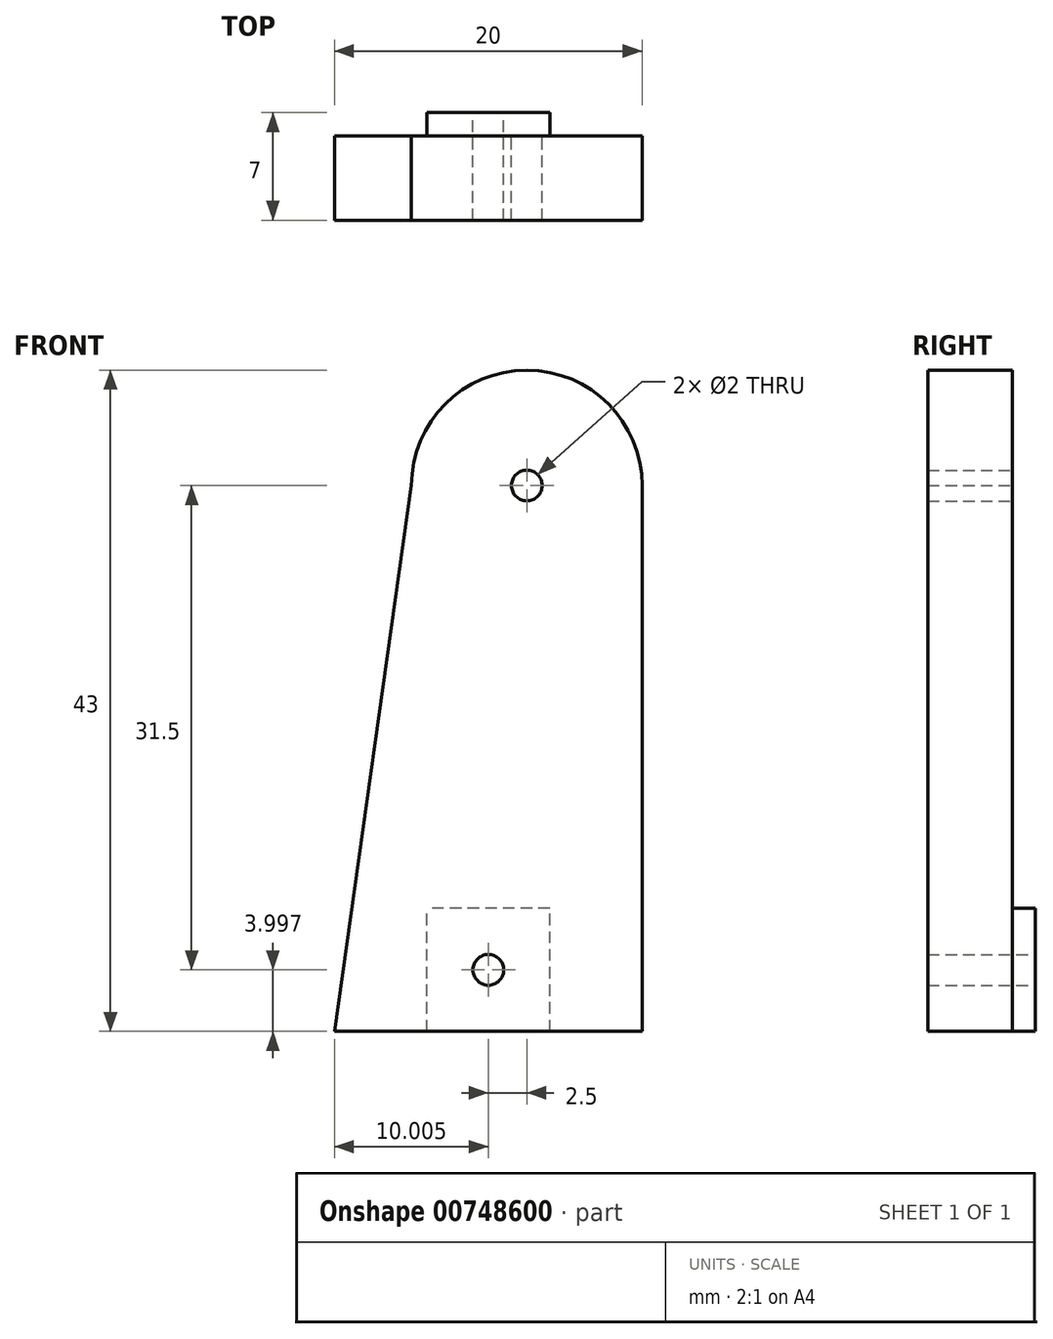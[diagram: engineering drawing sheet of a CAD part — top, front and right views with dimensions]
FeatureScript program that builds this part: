
annotation { "Feature Type Name" : "Feature", "Feature Type Description" : "" }
export const myFeature = defineFeature(function(context is Context, id is Id, definition is map)
    precondition{}
    {
        {
            var Q0;
            Q0=qCreatedBy(makeId("Front.planeOp"),FACE);
            var sketch = newSketch(context, id + "F0", { "sketchPlane" : qUnion([Q0])});
            skLineSegment(sketch, "E0.bottom", {"start": v(-52.7, 92.14) * mm, "end": v(-37.7, 92.14) * mm});
            skLineSegment(sketch, "E0.top", {"start": v(-52.7, -7.86) * mm, "end": v(-37.7, -7.86) * mm});
            skLineSegment(sketch, "E0.left", {"start": v(-52.7, 92.14) * mm, "end": v(-52.7, -7.86) * mm});
            skLineSegment(sketch, "E0.right", {"start": v(-37.7, 92.14) * mm, "end": v(-37.7, -7.86) * mm});
            skCircle(sketch, "E1", {"center": v(-45.2, 84.64) * mm, "radius": 1 * mm});
            skCircle(sketch, "E2", {"center": v(-45.2, 84.64) * mm, "radius": 7.5 * mm});
            skSolve(sketch);
        }
        {
            var Q0;
            Q0=makeQuery(id+"F0.imprint","IMPRINT",FACE,{"disambiguationData":[TD([[makeQuery(id+"F0.imprint","IMPRINT",EDGE,{"derivedFrom":sQuery(id+"F0.wireOp",EDGE,"E1")}),-1.0]])]});
            var Q1;
            {var subQ0=sQuery(id+"F0.wireOp",EDGE,"E0.top");Q1=makeQuery(id+"F0.imprint","IMPRINT",FACE,{"disambiguationData":[TD([[makeQuery(id+"F0.imprint","IMPRINT",EDGE,{"derivedFrom":subQ0}),1.0]])]});}
            extrude(context, id + "F1", {"entities" : qUnion([Q0, Q1]), "depth" : 5.5 * mm, "offsetDistance" : 25 * mm});
        }
        {
            var Q0;
            Q0=makeQuery(id+"F1.opExtrude","SWEPT_FACE",FACE,{"disambiguationData":[OSD([sQuery(id+"F0.wireOp",EDGE,"E0.left")])]});
            var sketch = newSketch(context, id + "F2", { "sketchPlane" : qUnion([Q0])});
            skLineSegment(sketch, "E3.bottom", {"start": v(0, 84.64) * mm, "end": v(5.5, 84.64) * mm});
            skLineSegment(sketch, "E3.top", {"start": v(0, 49.14) * mm, "end": v(5.5, 49.14) * mm});
            skLineSegment(sketch, "E3.left", {"start": v(0, 84.64) * mm, "end": v(0, 49.14) * mm});
            skLineSegment(sketch, "E3.right", {"start": v(5.5, 84.64) * mm, "end": v(5.5, 49.14) * mm});
            skSolve(sketch);
        }
        {
            var Q0;
            {var subQ0=sQuery(id+"F2.wireOp",EDGE,"E3.top");Q0=makeQuery(id+"F2.imprint","IMPRINT",FACE,{"disambiguationData":[TD([[makeQuery(id+"F2.imprint","IMPRINT",EDGE,{"derivedFrom":subQ0}),-1.0]])]});}
            extrude(context, id + "F3", {"entities" : qUnion([Q0]), "operationType" : NewBodyOperationType.REMOVE, "oppositeDirection" : true, "depth" : 25 * mm, "offsetDistance" : 25 * mm});
        }
        {
            var Q0;
            Q0=makeQuery(id+"F1.opExtrude","SWEPT_FACE",FACE,{"disambiguationData":[OSD([sQuery(id+"F0.wireOp",EDGE,"E0.left")])]});
            extrude(context, id + "F4", {"entities" : qUnion([Q0]), "operationType" : NewBodyOperationType.ADD, "depth" : 5 * mm, "offsetDistance" : 25 * mm});
        }
        {
            var Q0;
            {var subQ0=sQuery(id+"F0.wireOp",EDGE,"E0.left");Q0=makeQuery(id+"F4.boolean.opBoolean","MERGE",FACE,{"derivedFrom":[makeQuery(id+"F1.opExtrude","CAP_FACE",FACE,{"disambiguationData":[OSD([sQuery(id+"F0.wireOp",EDGE,"E0.top"),subQ0,sQuery(id+"F0.wireOp",EDGE,"E0.right"),sQuery(id+"F0.wireOp",EDGE,"E1"),sQuery(id+"F0.wireOp",EDGE,"E2")])],"isStart":false}),makeQuery(id+"F4.opExtrude","SWEPT_FACE",FACE,{"disambiguationData":[OSD([subQ0]),TDD([makeQuery(id+"F1.opExtrude","CAP_EDGE",EDGE,{"disambiguationData":[OSD([subQ0])],"isStart":false})])]})]});}
            var sketch = newSketch(context, id + "F5", { "sketchPlane" : qUnion([Q0])});
            skLineSegment(sketch, "E4", {"start": v(-52.7, 84.64) * mm, "end": v(-57.7, 49.14) * mm});
            skSolve(sketch);
        }
        {
            var Q0;
            Q0=makeQuery(id+"F5.imprint","IMPRINT",FACE,{"disambiguationData":[TD([[makeQuery(id+"F5.imprint","IMPRINT",EDGE,{"derivedFrom":sQuery(id+"F5.wireOp",EDGE,"E4")}),-1.0]])]});
            extrude(context, id + "F6", {"entities" : qUnion([Q0]), "operationType" : NewBodyOperationType.REMOVE, "oppositeDirection" : true, "depth" : 25 * mm, "offsetDistance" : 25 * mm});
        }
        {
            var Q0;
            {var subQ0=sQuery(id+"F0.wireOp",EDGE,"E0.left");Q0=makeQuery(id+"F4.boolean.opBoolean","MERGE",FACE,{"derivedFrom":[makeQuery(id+"F1.opExtrude","CAP_FACE",FACE,{"disambiguationData":[OSD([sQuery(id+"F0.wireOp",EDGE,"E0.top"),subQ0,sQuery(id+"F0.wireOp",EDGE,"E0.right"),sQuery(id+"F0.wireOp",EDGE,"E1"),sQuery(id+"F0.wireOp",EDGE,"E2")])],"isStart":true}),makeQuery(id+"F4.opExtrude","SWEPT_FACE",FACE,{"disambiguationData":[OSD([subQ0]),TDD([makeQuery(id+"F1.opExtrude","CAP_EDGE",EDGE,{"disambiguationData":[OSD([subQ0])],"isStart":true})])]})]});}
            var sketch = newSketch(context, id + "F7", { "sketchPlane" : qUnion([Q0])});
            skLineSegment(sketch, "E5.bottom", {"start": v(43.7, 49.14) * mm, "end": v(51.7, 49.14) * mm});
            skLineSegment(sketch, "E5.top", {"start": v(43.7, 57.14) * mm, "end": v(51.7, 57.14) * mm});
            skLineSegment(sketch, "E5.left", {"start": v(43.7, 49.14) * mm, "end": v(43.7, 57.14) * mm});
            skLineSegment(sketch, "E5.right", {"start": v(51.7, 49.14) * mm, "end": v(51.7, 57.14) * mm});
            skSolve(sketch);
        }
        {
            var Q0;
            Q0=makeQuery(id+"F7.imprint","IMPRINT",FACE,{"disambiguationData":[TD([[makeQuery(id+"F7.imprint","IMPRINT",EDGE,{"derivedFrom":sQuery(id+"F7.wireOp",EDGE,"E5.bottom")}),1.0]])]});
            extrude(context, id + "F8", {"entities" : qUnion([Q0]), "operationType" : NewBodyOperationType.ADD, "depth" : 1.5 * mm, "offsetDistance" : 25 * mm});
        }
        {
            var Q0;
            Q0=makeQuery(id+"F8.opExtrude","CAP_FACE",FACE,{"disambiguationData":[OSD([sQuery(id+"F7.wireOp",EDGE,"E5.bottom"),sQuery(id+"F7.wireOp",EDGE,"E5.top"),sQuery(id+"F7.wireOp",EDGE,"E5.left"),sQuery(id+"F7.wireOp",EDGE,"E5.right")])],"isStart":false});
            var sketch = newSketch(context, id + "F9", { "sketchPlane" : qUnion([Q0])});
            skCircle(sketch, "E6", {"center": v(47.7, 53.14) * mm, "radius": 1 * mm});
            skPoint(sketch, "E6.centerSnap0", {"position": v(51.7, 53.14) * mm});
            skPoint(sketch, "E6.centerSnap1", {"position": v(47.7, 57.14) * mm});
            skSolve(sketch);
        }
        {
            var Q0;
            Q0=makeQuery(id+"F9.imprint","IMPRINT",FACE,{"disambiguationData":[TD([[makeQuery(id+"F9.imprint","IMPRINT",EDGE,{"derivedFrom":sQuery(id+"F9.wireOp",EDGE,"E6")}),1.0]])]});
            extrude(context, id + "F10", {"entities" : qUnion([Q0]), "operationType" : NewBodyOperationType.REMOVE, "oppositeDirection" : true, "depth" : 25 * mm, "offsetDistance" : 25 * mm});
        }
    });
